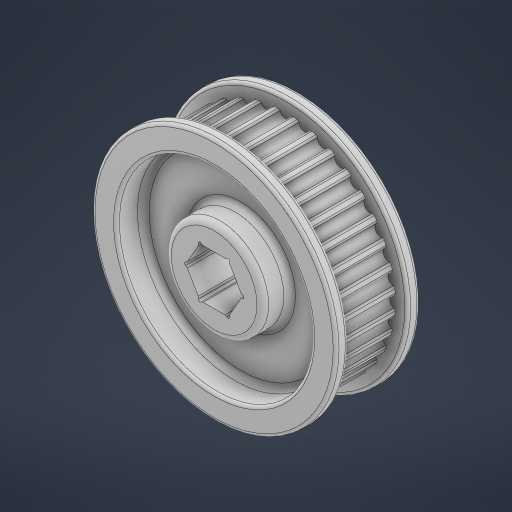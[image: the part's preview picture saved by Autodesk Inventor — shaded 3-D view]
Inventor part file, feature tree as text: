
AUTODESK INVENTOR PART (.ipt)
format: ipt  version: 2023.1 (Build 271208000, 208)  size: 611,840 bytes
history: native  units: in
note: dims shown in document units (in); Inventor stores cm internally (conversion verified against a paired STEP export)
features: fillet x6, extrude x5, sketch x3, other x2, plane x2, mirror x2, pattern_circular x1
ambient origin geometry x8: Origin, YZ Plane, XZ Plane, XY Plane, X Axis, Y Axis, Z Axis, Center Point
bodies: Solid1 (feature_tree)
feature tree (21):
  other  "Pitch Diameter"
  extrude  "Extrusion1"  Depth=2.2557in
  extrude  "Extrusion3"  TaperAngle=360.0deg  [1 undecoded]
  fillet  "Fillet1"  Radius=0.0685in
  pattern_circular  "Circular Pattern1"  [2 undecoded]
  plane  "Work Plane1"
  extrude  "Extrusion4"  TaperAngle=0.0deg  [1 undecoded]
  mirror  "Mirror1"
  fillet  "Fillet2"  Radius=0.0197in
  extrude  "Extrusion5"  Depth=0.5in
  fillet  "Fillet3"  [1 undecoded]
  extrude  "Extrusion6"  Depth=0.5in
  mirror  "Mirror2"
  fillet  "Fillet4"  Radius=0.125in
  fillet  "Fillet5"  Radius=0.03in
  fillet  "Fillet6"  Radius=0.503in
  other  "TeethCut"
  sketch  "Sketch4"  dims[d2=0.1201in d7=2.2557in]
  sketch  "Sketch5"  dims[d8=14.1732in d10=360.0deg d12=0.0685in]
  sketch  "Sketch6"  dims[d13=2.2557in d14=0.6102in d15=0.0in d18=0.0in d19=0.0in d20=0.0197in d21=14.1732in d22=360.0deg d26=2.5057in d27=0.125in d28=0.0in d29=0.03in d30=0.503in d31=0.03in d32=0.0in d33=0.0in d34=0.03in d35=1.0in d36=2.0057in d37=0.2756in d38=0.0in d39=0.03in d40=0.06in d41=0.06in d24=0.5in d25=0.0344in]
  plane  "Work Plane2"
note: 5 required parameter values undecoded (feature->parameter linkage not recoverable at this tier; creation-order binding heuristic only, values carry confidence <= 0.55)
